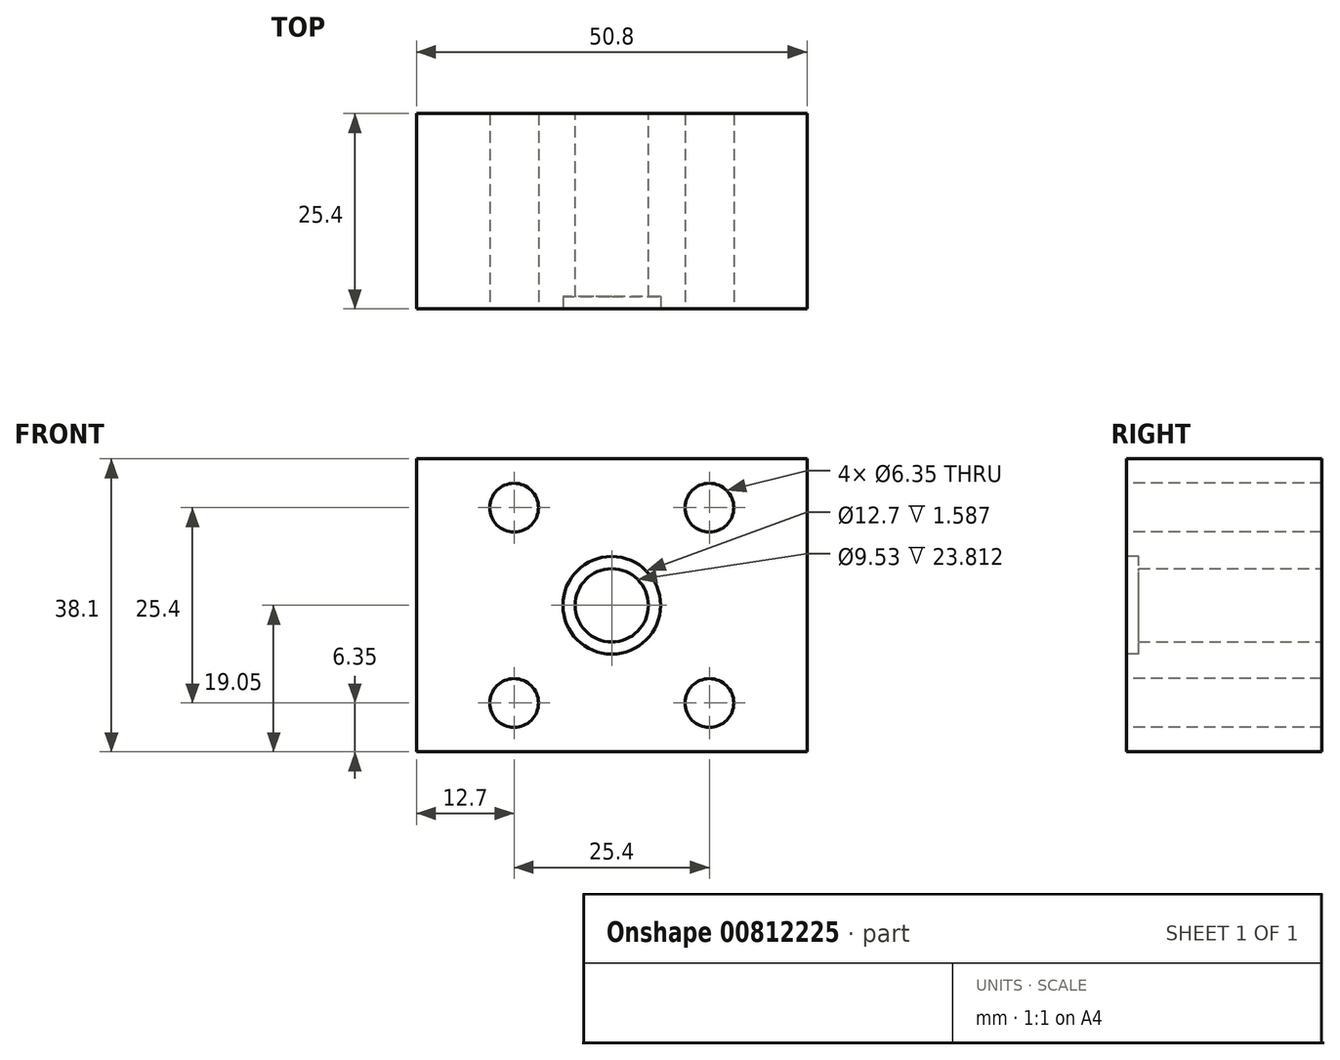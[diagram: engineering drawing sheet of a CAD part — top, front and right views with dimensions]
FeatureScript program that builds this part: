
annotation { "Feature Type Name" : "Feature", "Feature Type Description" : "" }
export const myFeature = defineFeature(function(context is Context, id is Id, definition is map)
    precondition{}
    {
        {
            var Q0;
            Q0=qCreatedBy(makeId("Right.planeOp"),FACE);
            var sketch = newSketch(context, id + "F0", { "sketchPlane" : qUnion([Q0])});
            skLineSegment(sketch, "E0.bottom", {"start": v(-12.7, 19.05) * mm, "end": v(12.7, 19.05) * mm});
            skLineSegment(sketch, "E0.top", {"start": v(-12.7, -19.05) * mm, "end": v(12.7, -19.05) * mm});
            skLineSegment(sketch, "E0.left", {"start": v(-12.7, 19.05) * mm, "end": v(-12.7, -19.05) * mm});
            skLineSegment(sketch, "E0.right", {"start": v(12.7, 19.05) * mm, "end": v(12.7, -19.05) * mm});
            skPoint(sketch, "E0.middle", {"position": v(0, 0) * mm});
            skSolve(sketch);
        }
        {
            var Q0;
            Q0=makeQuery(id+"F0.imprint","IMPRINT",FACE,{"disambiguationData":[TD([[makeQuery(id+"F0.imprint","IMPRINT",EDGE,{"derivedFrom":sQuery(id+"F0.wireOp",EDGE,"E0.bottom")}),-1.0]])]});
            extrude(context, id + "F1", {"entities" : qUnion([Q0]), "depth" : 50.8 * mm, "offsetDistance" : 25.4 * mm});
        }
        {
            var Q0;
            Q0=makeQuery(id+"F1.opExtrude","SWEPT_FACE",FACE,{"disambiguationData":[OSD([sQuery(id+"F0.wireOp",EDGE,"E0.left")])]});
            var sketch = newSketch(context, id + "F2", { "sketchPlane" : qUnion([Q0])});
            skLineSegment(sketch, "E1.bottom", {"start": v(12.7, 12.7) * mm, "end": v(38.1, 12.7) * mm, "construction": true});
            skLineSegment(sketch, "E1.top", {"start": v(12.7, -12.7) * mm, "end": v(38.1, -12.7) * mm, "construction": true});
            skLineSegment(sketch, "E1.left", {"start": v(12.7, 12.7) * mm, "end": v(12.7, -12.7) * mm, "construction": true});
            skLineSegment(sketch, "E1.right", {"start": v(38.1, 12.7) * mm, "end": v(38.1, -12.7) * mm, "construction": true});
            skPoint(sketch, "E1.middle", {"position": v(25.4, 0) * mm});
            skPoint(sketch, "E1.middle.positionSnap0", {"position": v(25.4, 19.05) * mm});
            skPoint(sketch, "E1.centerSnap0", {"position": v(25.4, 19.05) * mm});
            skCircle(sketch, "E2", {"center": v(12.7, 12.7) * mm, "radius": 3.18 * mm});
            skCircle(sketch, "E3", {"center": v(38.1, -12.7) * mm, "radius": 3.18 * mm});
            skCircle(sketch, "E4", {"center": v(38.1, 12.7) * mm, "radius": 3.18 * mm});
            skCircle(sketch, "E5", {"center": v(12.7, -12.7) * mm, "radius": 3.18 * mm});
            skSolve(sketch);
        }
        {
            var Q0;
            Q0=qSketchRegion(id+"F2",true);
            extrude(context, id + "F3", {"entities" : qUnion([Q0]), "operationType" : NewBodyOperationType.REMOVE, "oppositeDirection" : true, "depth" : 25.4 * mm, "offsetDistance" : 25.4 * mm});
        }
        {
            var Q0;
            Q0=makeQuery(id+"F1.opExtrude","SWEPT_FACE",FACE,{"disambiguationData":[OSD([sQuery(id+"F0.wireOp",EDGE,"E0.left")])]});
            var sketch = newSketch(context, id + "F4", { "sketchPlane" : qUnion([Q0])});
            skCircle(sketch, "E6", {"center": v(25.4, 0) * mm, "radius": 6.35 * mm});
            skLineSegment(sketch, "E7", {"start": v(25.4, 0) * mm, "end": v(0, 0) * mm, "construction": true});
            skLineSegment(sketch, "E8", {"start": v(25.4, 0) * mm, "end": v(25.4, 19.05) * mm, "construction": true});
            skSolve(sketch);
        }
        {
            var Q0;
            Q0 = qSketchRegion(id + "F4", true);
            extrude(context, id + "F5", {"entities" : qUnion([Q0]), "operationType" : NewBodyOperationType.REMOVE, "oppositeDirection" : true, "depth" : 1.59 * mm, "offsetDistance" : 25.4 * mm});
        }
        {
            var Q0;
            Q0=makeQuery(id+"F1.opExtrude","SWEPT_FACE",FACE,{"disambiguationData":[OSD([sQuery(id+"F0.wireOp",EDGE,"E0.right")])]});
            var sketch = newSketch(context, id + "F6", { "sketchPlane" : qUnion([Q0])});
            skCircle(sketch, "E9", {"center": v(-25.4, 0) * mm, "radius": 4.76 * mm});
            skLineSegment(sketch, "E10", {"start": v(-25.4, 0) * mm, "end": v(0, 0) * mm, "construction": true});
            skLineSegment(sketch, "E11", {"start": v(-25.4, 0) * mm, "end": v(-25.4, 19.05) * mm, "construction": true});
            skSolve(sketch);
        }
        {
            var Q0;
            Q0=makeQuery(id+"F6.imprint","IMPRINT",FACE,{"disambiguationData":[TD([[makeQuery(id+"F6.imprint","IMPRINT",EDGE,{"derivedFrom":sQuery(id+"F6.wireOp",EDGE,"E9")}),1.0]])]});
            extrude(context, id + "F7", {"entities" : qUnion([Q0]), "operationType" : NewBodyOperationType.REMOVE, "oppositeDirection" : true, "depth" : 25.4 * mm, "offsetDistance" : 25.4 * mm});
        }
    });
